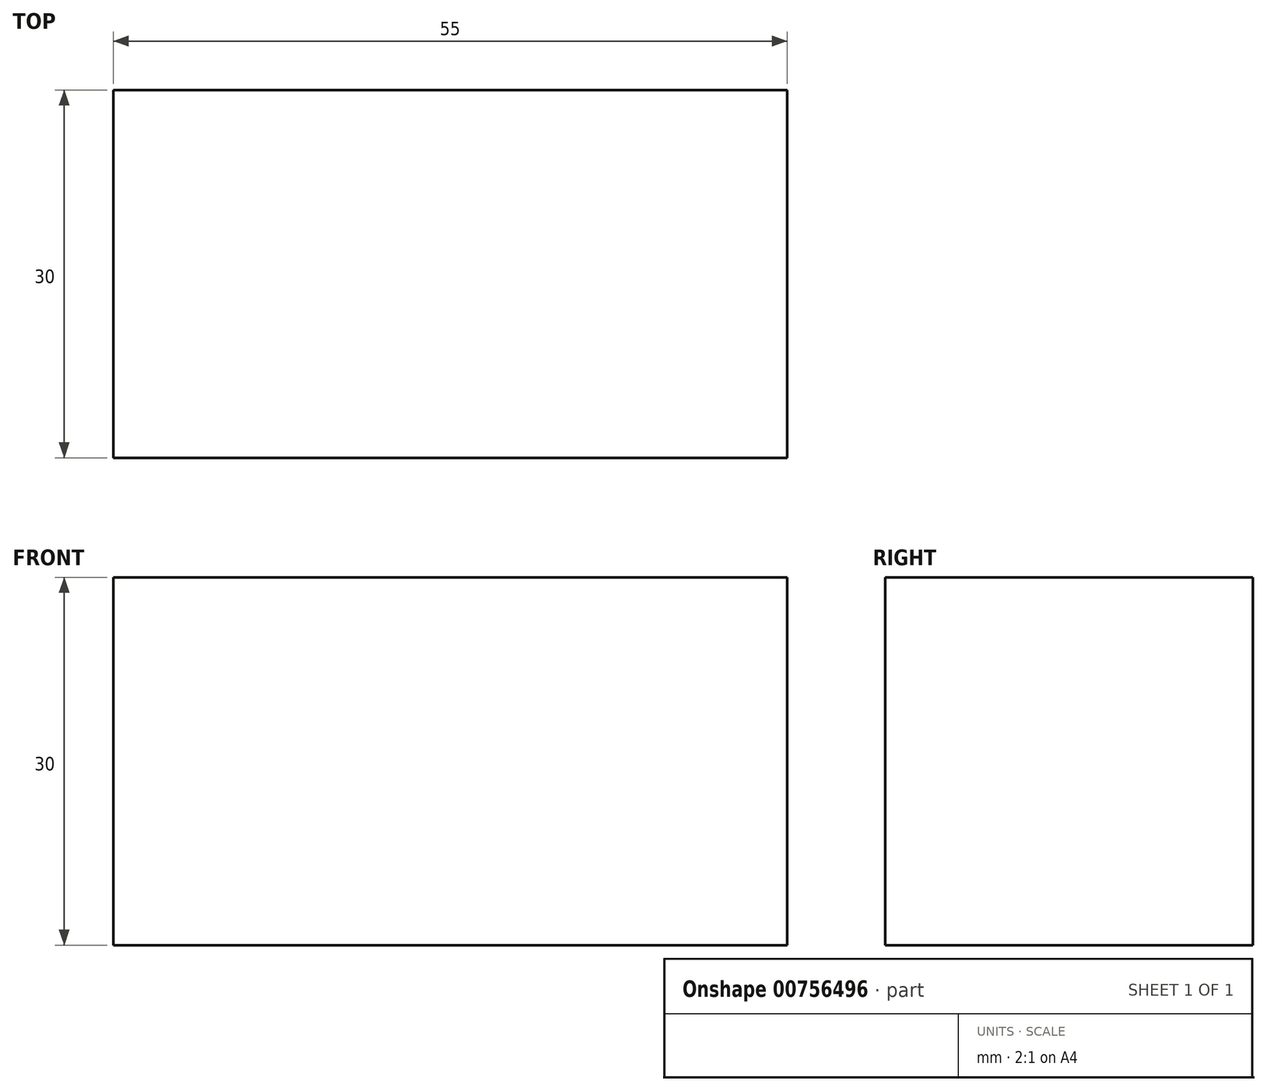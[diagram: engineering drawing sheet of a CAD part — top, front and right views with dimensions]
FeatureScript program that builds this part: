
annotation { "Feature Type Name" : "Feature", "Feature Type Description" : "" }
export const myFeature = defineFeature(function(context is Context, id is Id, definition is map)
    precondition{}
    {
        {
            var Q0;
            Q0=qCreatedBy(makeId("Front.planeOp"),FACE);
            var sketch = newSketch(context, id + "F0", { "sketchPlane" : qUnion([Q0])});
            skLineSegment(sketch, "E0.bottom", {"start": v(-31.67, 25.2) * mm, "end": v(23.33, 25.2) * mm});
            skLineSegment(sketch, "E0.top", {"start": v(-31.67, -4.8) * mm, "end": v(23.33, -4.8) * mm});
            skLineSegment(sketch, "E0.left", {"start": v(-31.67, 25.2) * mm, "end": v(-31.67, -4.8) * mm});
            skLineSegment(sketch, "E0.right", {"start": v(23.33, 25.2) * mm, "end": v(23.33, -4.8) * mm});
            skSolve(sketch);
        }
        {
            var Q0;
            Q0 = qSketchRegion(id + "F0", true);
            extrude(context, id + "F1", {"entities" : qUnion([Q0]), "depth" : 30 * mm, "offsetDistance" : 25 * mm});
        }
    });
